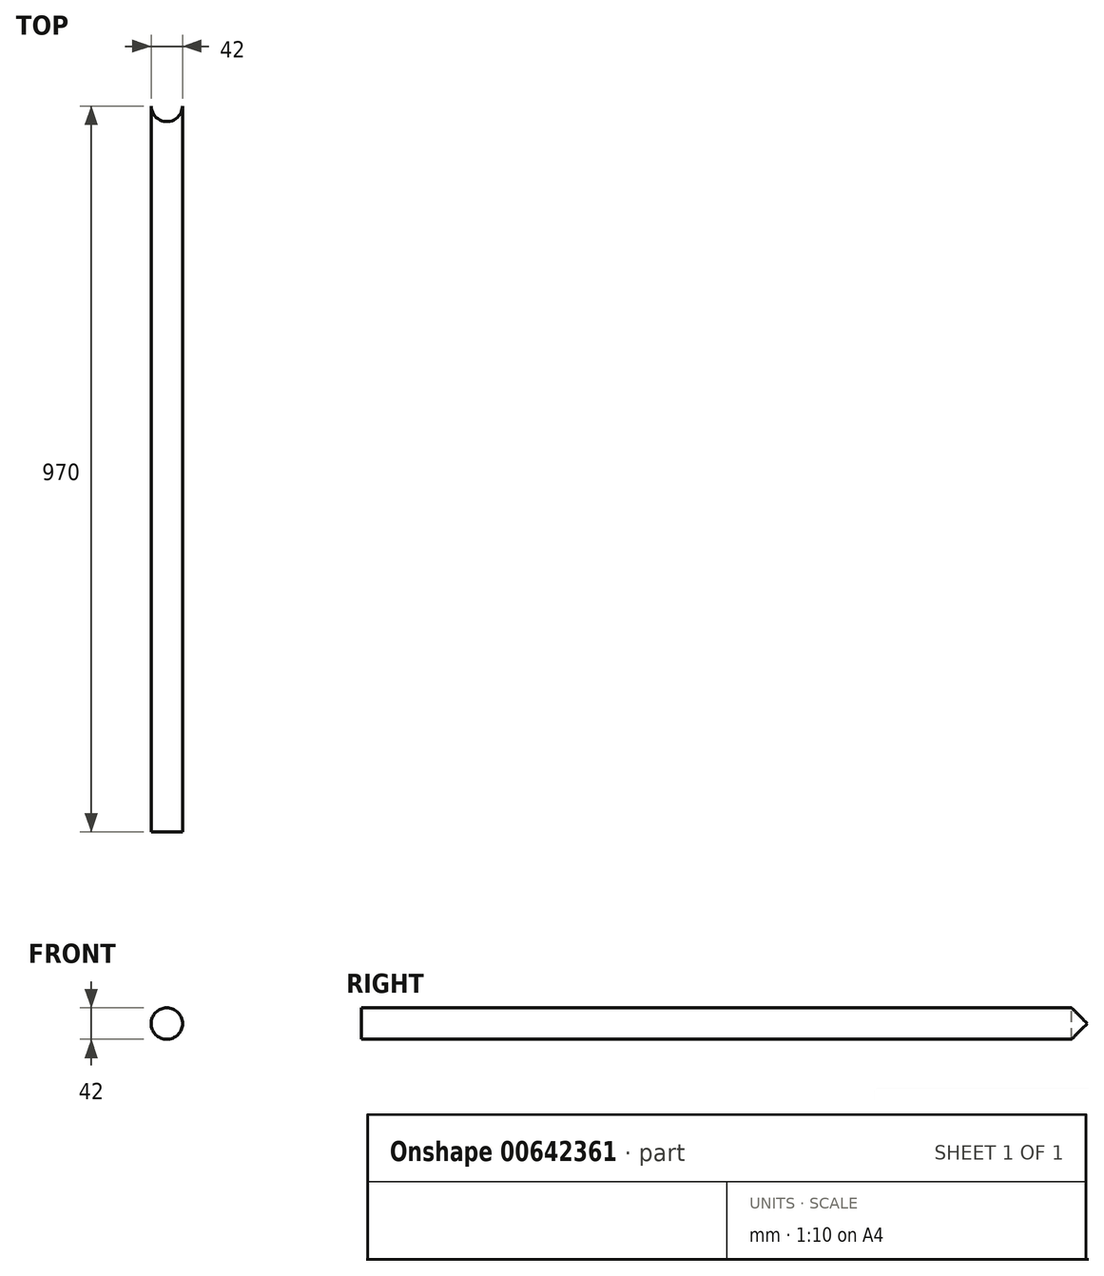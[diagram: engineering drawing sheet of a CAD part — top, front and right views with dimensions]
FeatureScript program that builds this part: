
annotation { "Feature Type Name" : "Feature", "Feature Type Description" : "" }
export const myFeature = defineFeature(function(context is Context, id is Id, definition is map)
    precondition{}
    {
        {
            var Q0;
            Q0=qCreatedBy(makeId("Front.planeOp"),FACE);
            var sketch = newSketch(context, id + "F0", { "sketchPlane" : qUnion([Q0])});
            skCircle(sketch, "E0", {"center": v(0, 0) * mm, "radius": 21 * mm});
            skSolve(sketch);
        }
        {
            var Q0;
            Q0=makeQuery(id+"F0.imprint","IMPRINT",FACE,{"disambiguationData":[TD([[makeQuery(id+"F0.imprint","IMPRINT",EDGE,{"derivedFrom":sQuery(id+"F0.wireOp",EDGE,"E0")}),1.0]])]});
            extrude(context, id + "F1", {"entities" : qUnion([Q0]), "depth" : 970 * mm, "offsetDistance" : 25 * mm});
        }
        {
            var Q0;
            Q0=qCreatedBy(makeId("Top.planeOp"),FACE);
            var sketch = newSketch(context, id + "F2", { "sketchPlane" : qUnion([Q0])});
            skLineSegment(sketch, "E1", {"start": v(-21, 0) * mm, "end": v(0, 0) * mm});
            skLineSegment(sketch, "E2", {"start": v(0, 0) * mm, "end": v(21, 0) * mm});
            skCircle(sketch, "E3", {"center": v(0, 0) * mm, "radius": 21 * mm});
            skSolve(sketch);
        }
        {
            var Q0;
            Q0=qSketchRegion(id+"F2",true);
            extrude(context, id + "F3", {"entities" : qUnion([Q0]), "operationType" : NewBodyOperationType.REMOVE, "endBound" : BoundingType.SYMMETRIC, "oppositeDirection" : true, "depth" : 1000 * mm, "offsetDistance" : 25 * mm});
        }
    });
